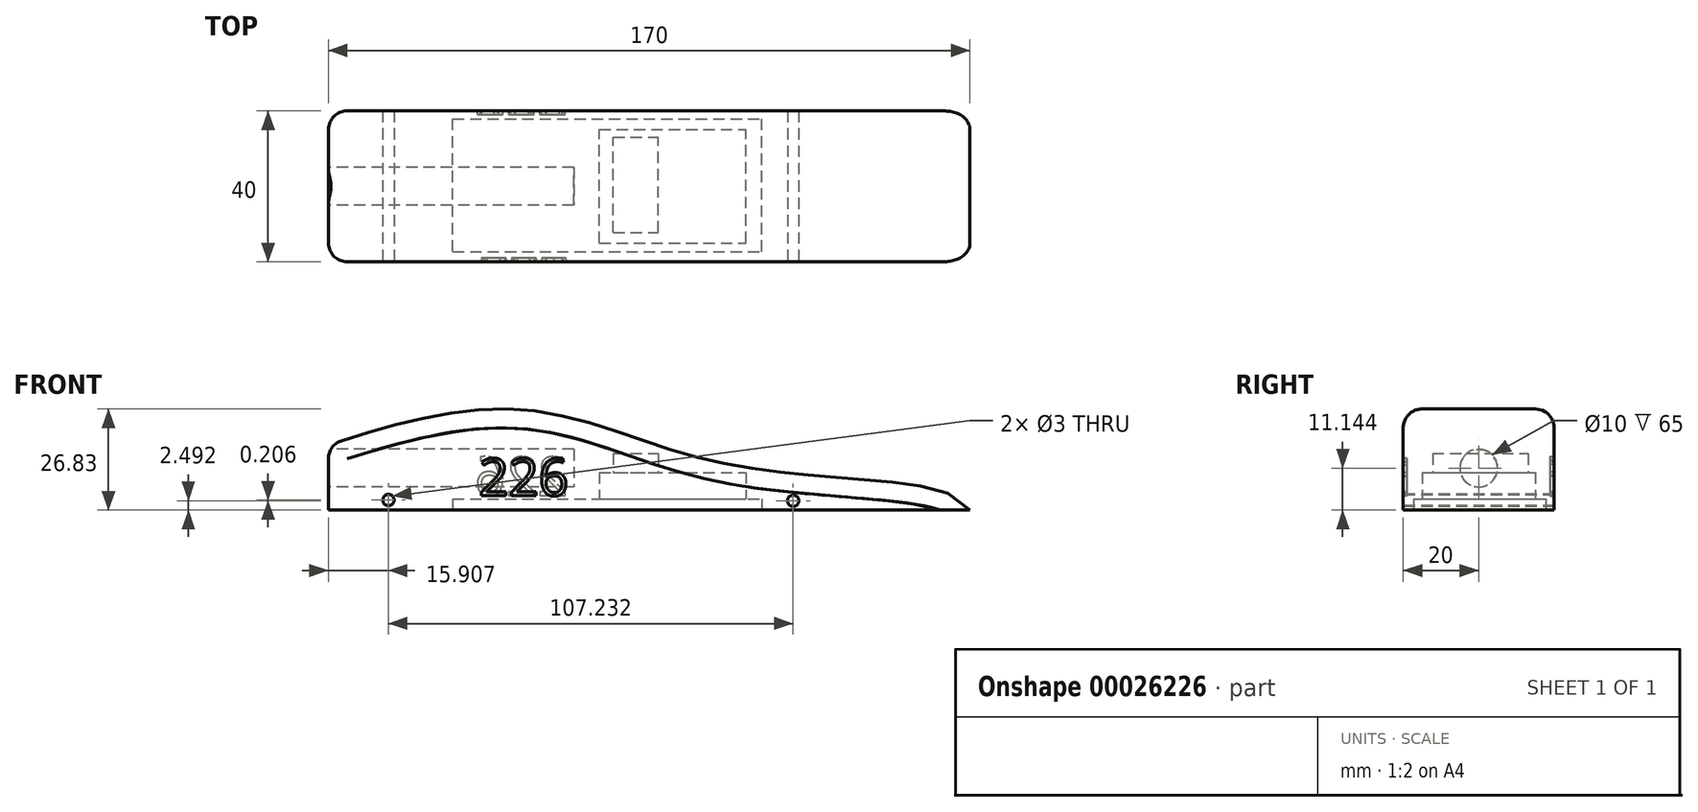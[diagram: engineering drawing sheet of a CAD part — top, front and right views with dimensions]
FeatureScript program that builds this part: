
annotation { "Feature Type Name" : "Feature", "Feature Type Description" : "" }
export const myFeature = defineFeature(function(context is Context, id is Id, definition is map)
    precondition{}
    {
        {
            var Q0;
            Q0=qCreatedBy(makeId("Front.planeOp"),FACE);
            var sketch = newSketch(context, id + "F0", { "sketchPlane" : qUnion([Q0])});
            skLineSegment(sketch, "E0.bottom", {"start": v(-234.2, -32.3) * mm, "end": v(-64.2, -32.3) * mm});
            skLineSegment(sketch, "E0.top", {"start": v(-234.2, 37.7) * mm, "end": v(-64.2, 37.7) * mm});
            skLineSegment(sketch, "E0.left", {"start": v(-234.2, -32.3) * mm, "end": v(-234.2, 37.7) * mm});
            skLineSegment(sketch, "E0.right", {"start": v(-64.2, -32.3) * mm, "end": v(-64.2, 37.7) * mm});
            skFitSpline(sketch, "E1", {"points": [v(-64.2, -32.3) * mm, v(-71.26, -27.3) * mm, v(-123.6, -20.98) * mm, v(-160.3, -10.62) * mm, v(-185.43, -5.52) * mm, v(-211.6, -8.5) * mm, v(-234.2, -15) * mm], "startDerivative": vector(-49.72, 58.88) * mm, "endDerivative": vector(-142.42, -45.35) * mm});
            skSolve(sketch);
        }
        {
            var Q0;
            Q0=makeQuery(id+"F0.imprint","IMPRINT",FACE,{"disambiguationData":[TD([[makeQuery(id+"F0.imprint","IMPRINT",EDGE,{"derivedFrom":sQuery(id+"F0.wireOp",EDGE,"E0.bottom")}),1.0]])]});
            extrude(context, id + "F1", {"entities" : qUnion([Q0]), "depth" : 40 * mm});
        }
        {
            var Q0;
            Q0=makeQuery(id+"F1.opExtrude","SWEPT_FACE",FACE,{"disambiguationData":[OSD([sQuery(id+"F0.wireOp",EDGE,"E0.left")])]});
            var sketch = newSketch(context, id + "F2", { "sketchPlane" : qUnion([Q0])});
            skCircle(sketch, "E2", {"center": v(20, -21.16) * mm, "radius": 5 * mm});
            skSolve(sketch);
        }
        {
            var Q0;
            Q0=makeQuery(id+"F2.imprint","IMPRINT",FACE,{"disambiguationData":[TD([[makeQuery(id+"F2.imprint","IMPRINT",EDGE,{"derivedFrom":sQuery(id+"F2.wireOp",EDGE,"E2")}),1.0]])]});
            extrude(context, id + "F3", {"entities" : qUnion([Q0]), "operationType" : NewBodyOperationType.REMOVE, "oppositeDirection" : true, "depth" : 65 * mm});
        }
        {
            var Q0;
            Q0=makeQuery(id+"F1.opExtrude","CAP_EDGE",EDGE,{"disambiguationData":[OSD([sQuery(id+"F0.wireOp",EDGE,"E1")])],"isStart":false});
            var Q1;
            Q1=makeQuery(id+"F1.opExtrude","CAP_EDGE",EDGE,{"disambiguationData":[OSD([sQuery(id+"F0.wireOp",EDGE,"E1")])],"isStart":true});
            var Q2;
            Q2=makeQuery(id+"F1.opExtrude","SWEPT_EDGE",EDGE,{"disambiguationData":[OSD([sQuery(id+"F0.wireOp",EDGE,"E0.left"),sQuery(id+"F0.wireOp",EDGE,"E1")])]});
            var Q3;
            Q3=makeQuery(id+"F1.opExtrude","CAP_EDGE",EDGE,{"disambiguationData":[OSD([sQuery(id+"F0.wireOp",EDGE,"E0.left")])],"isStart":false});
            var Q4;
            Q4=makeQuery(id+"F1.opExtrude","CAP_EDGE",EDGE,{"disambiguationData":[OSD([sQuery(id+"F0.wireOp",EDGE,"E0.left")])],"isStart":true});
            fillet(context, id + "F4", {"entities" : qUnion([Q0, Q1, Q2, Q3, Q4]), "radius" : 5 * mm, "tangentPropagation" : true, "allowEdgeOverflow" : false});
        }
        {
            var Q0;
            Q0=makeQuery(id+"F1.opExtrude","SWEPT_FACE",FACE,{"disambiguationData":[OSD([sQuery(id+"F0.wireOp",EDGE,"E0.bottom")])]});
            var sketch = newSketch(context, id + "F5", { "sketchPlane" : qUnion([Q0])});
            skLineSegment(sketch, "E3.bottom", {"start": v(-201.24, 37.3) * mm, "end": v(-119.38, 37.3) * mm});
            skLineSegment(sketch, "E3.top", {"start": v(-201.24, 2.17) * mm, "end": v(-119.38, 2.17) * mm});
            skLineSegment(sketch, "E3.left", {"start": v(-201.24, 37.3) * mm, "end": v(-201.24, 2.17) * mm});
            skLineSegment(sketch, "E3.right", {"start": v(-119.38, 37.3) * mm, "end": v(-119.38, 2.17) * mm});
            skSolve(sketch);
        }
        {
            var Q0;
            Q0=makeQuery(id+"F5.imprint","IMPRINT",FACE,{"disambiguationData":[TD([[makeQuery(id+"F5.imprint","IMPRINT",EDGE,{"derivedFrom":sQuery(id+"F5.wireOp",EDGE,"E3.bottom")}),-1.0]])]});
            extrude(context, id + "F6", {"entities" : qUnion([Q0]), "operationType" : NewBodyOperationType.REMOVE, "oppositeDirection" : true, "depth" : 3 * mm});
        }
        {
            var Q0;
            Q0=makeQuery(id+"F1.opExtrude","SWEPT_FACE",FACE,{"disambiguationData":[OSD([sQuery(id+"F0.wireOp",EDGE,"E0.bottom")])]});
            var sketch = newSketch(context, id + "F7", { "sketchPlane" : qUnion([Q0])});
            skLineSegment(sketch, "E4.bottom", {"start": v(-162.42, 35.02) * mm, "end": v(-123.6, 35.02) * mm});
            skLineSegment(sketch, "E4.top", {"start": v(-162.42, 4.98) * mm, "end": v(-123.6, 4.98) * mm});
            skLineSegment(sketch, "E4.left", {"start": v(-162.42, 35.02) * mm, "end": v(-162.42, 4.98) * mm});
            skLineSegment(sketch, "E4.right", {"start": v(-123.6, 35.02) * mm, "end": v(-123.6, 4.98) * mm});
            skSolve(sketch);
        }
        {
            var Q0;
            Q0=makeQuery(id+"F7.imprint","IMPRINT",FACE,{"disambiguationData":[TD([[makeQuery(id+"F7.imprint","IMPRINT",EDGE,{"derivedFrom":sQuery(id+"F7.wireOp",EDGE,"E4.bottom")}),-1.0]])]});
            extrude(context, id + "F8", {"entities" : qUnion([Q0]), "operationType" : NewBodyOperationType.REMOVE, "oppositeDirection" : true, "depth" : 10 * mm});
        }
        {
            var Q0;
            Q0=makeQuery(id+"F8.boolean.opBoolean","COPY",FACE,{"derivedFrom":makeQuery(id+"F8.opExtrude","CAP_FACE",FACE,{"disambiguationData":[OSD([sQuery(id+"F7.wireOp",EDGE,"E4.bottom"),sQuery(id+"F7.wireOp",EDGE,"E4.top"),sQuery(id+"F7.wireOp",EDGE,"E4.left"),sQuery(id+"F7.wireOp",EDGE,"E4.right")])],"isStart":false})});
            var sketch = newSketch(context, id + "F9", { "sketchPlane" : qUnion([Q0])});
            skLineSegment(sketch, "E5.bottom", {"start": v(-158.73, 32.2) * mm, "end": v(-146.78, 32.2) * mm});
            skLineSegment(sketch, "E5.top", {"start": v(-158.73, 6.91) * mm, "end": v(-146.78, 6.91) * mm});
            skLineSegment(sketch, "E5.left", {"start": v(-158.73, 32.2) * mm, "end": v(-158.73, 6.91) * mm});
            skLineSegment(sketch, "E5.right", {"start": v(-146.78, 32.2) * mm, "end": v(-146.78, 6.91) * mm});
            skSolve(sketch);
        }
        {
            var Q0;
            Q0=makeQuery(id+"F9.imprint","IMPRINT",FACE,{"disambiguationData":[TD([[makeQuery(id+"F9.imprint","IMPRINT",EDGE,{"derivedFrom":sQuery(id+"F9.wireOp",EDGE,"E5.bottom")}),-1.0]])]});
            extrude(context, id + "F10", {"entities" : qUnion([Q0]), "operationType" : NewBodyOperationType.REMOVE, "oppositeDirection" : true, "depth" : 5 * mm});
        }
        {
            var Q0;
            Q0=makeQuery(id+"F1.opExtrude","CAP_FACE",FACE,{"disambiguationData":[OSD([sQuery(id+"F0.wireOp",EDGE,"E0.bottom"),sQuery(id+"F0.wireOp",EDGE,"E0.left"),sQuery(id+"F0.wireOp",EDGE,"E1")])],"isStart":false});
            var sketch = newSketch(context, id + "F11", { "sketchPlane" : qUnion([Q0])});
            skCircle(sketch, "E6", {"center": v(-111.06, -29.8) * mm, "radius": 1.5 * mm});
            skSolve(sketch);
        }
        {
            var Q0;
            Q0=makeQuery(id+"F11.imprint","IMPRINT",FACE,{"disambiguationData":[TD([[makeQuery(id+"F11.imprint","IMPRINT",EDGE,{"derivedFrom":sQuery(id+"F11.wireOp",EDGE,"E6")}),-1.0]])]});
            var sketch = newSketch(context, id + "F12", { "sketchPlane" : qUnion([Q0])});
            skCircle(sketch, "E7", {"center": v(-218.3, -29.6) * mm, "radius": 1.5 * mm});
            skSolve(sketch);
        }
        {
            var Q0;
            Q0=makeQuery(id+"F11.imprint","IMPRINT",FACE,{"disambiguationData":[TD([[makeQuery(id+"F11.imprint","IMPRINT",EDGE,{"derivedFrom":sQuery(id+"F11.wireOp",EDGE,"E6")}),1.0]])]});
            extrude(context, id + "F13", {"entities" : qUnion([Q0]), "operationType" : NewBodyOperationType.REMOVE, "endBound" : BoundingType.THROUGH_ALL, "oppositeDirection" : true, "depth" : 25 * mm});
        }
        {
            var Q0;
            Q0=makeQuery(id+"F12.imprint","IMPRINT",FACE,{"disambiguationData":[TD([[makeQuery(id+"F12.imprint","IMPRINT",EDGE,{"derivedFrom":sQuery(id+"F12.wireOp",EDGE,"E7")}),1.0]])]});
            extrude(context, id + "F14", {"entities" : qUnion([Q0]), "operationType" : NewBodyOperationType.REMOVE, "endBound" : BoundingType.THROUGH_ALL, "oppositeDirection" : true, "depth" : 25 * mm});
        }
        {
            var Q0;
            Q0=makeQuery(id+"F1.opExtrude","CAP_FACE",FACE,{"disambiguationData":[OSD([sQuery(id+"F0.wireOp",EDGE,"E0.bottom"),sQuery(id+"F0.wireOp",EDGE,"E0.left"),sQuery(id+"F0.wireOp",EDGE,"E1")])],"isStart":false});
            var sketch = newSketch(context, id + "F15", { "sketchPlane" : qUnion([Q0])});
            skText(sketch, "E8", { "text": "226", "fontName": "OpenSans-Regular.ttf"});
            const initialGuessF15  = {"E8": [-0.1943, -0.02848, 1, 0, 0.00995]};
            skSetInitialGuess(sketch, initialGuessF15);
            skSolve(sketch);
        }
        {
            var Q0;
            Q0 = qSketchRegion(id + "F15", true);
            extrude(context, id + "F16", {"entities" : qUnion([Q0]), "operationType" : NewBodyOperationType.REMOVE, "oppositeDirection" : true, "depth" : 1 * mm});
        }
        {
            var Q0;
            Q0=makeQuery(id+"F1.opExtrude","CAP_FACE",FACE,{"disambiguationData":[OSD([sQuery(id+"F0.wireOp",EDGE,"E0.bottom"),sQuery(id+"F0.wireOp",EDGE,"E0.left"),sQuery(id+"F0.wireOp",EDGE,"E1")])],"isStart":true});
            var sketch = newSketch(context, id + "F17", { "sketchPlane" : qUnion([Q0])});
            skText(sketch, "E9", { "text": "226\n", "fontName": "OpenSans-Regular.ttf"});
            const initialGuessF17  = {"E9": [0.17074, -0.02847, 1, 0, 0.01035]};
            skSetInitialGuess(sketch, initialGuessF17);
            skSolve(sketch);
        }
        {
            var Q0;
            Q0 = qSketchRegion(id + "F17", true);
            extrude(context, id + "F18", {"entities" : qUnion([Q0]), "operationType" : NewBodyOperationType.REMOVE, "oppositeDirection" : true, "depth" : 1 * mm});
        }
    });
